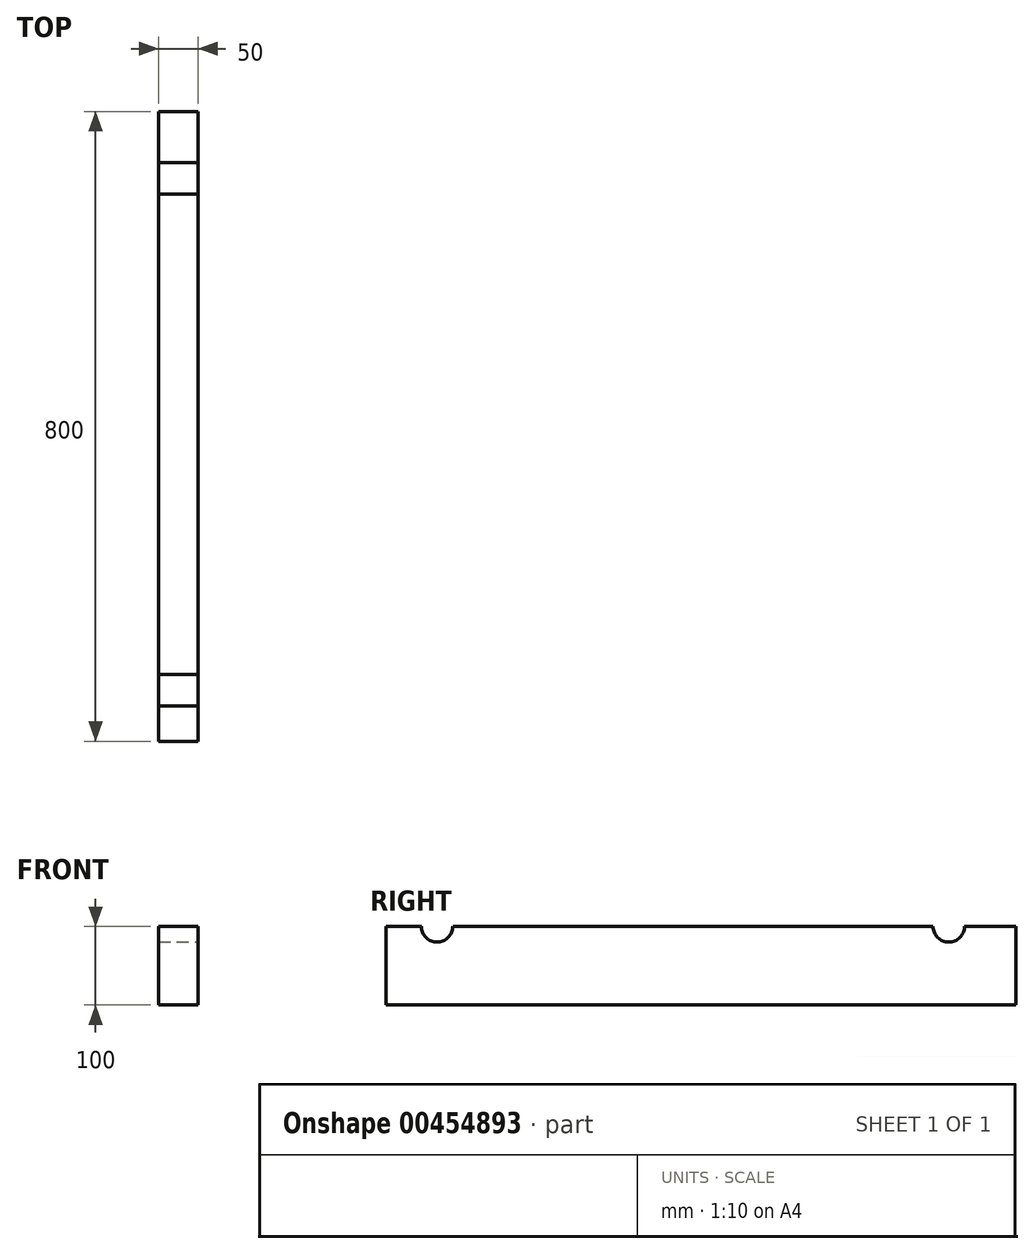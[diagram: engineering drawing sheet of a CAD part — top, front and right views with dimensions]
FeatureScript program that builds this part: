
annotation { "Feature Type Name" : "Feature", "Feature Type Description" : "" }
export const myFeature = defineFeature(function(context is Context, id is Id, definition is map)
    precondition{}
    {
        {
            var Q0;
            Q0=qCreatedBy(makeId("Front.planeOp"),FACE);
            var sketch = newSketch(context, id + "F0", { "sketchPlane" : qUnion([Q0])});
            skLineSegment(sketch, "E0.bottom", {"start": v(0, 0) * mm, "end": v(50, 0) * mm});
            skLineSegment(sketch, "E0.top", {"start": v(0, 100) * mm, "end": v(50, 100) * mm});
            skLineSegment(sketch, "E0.left", {"start": v(0, 0) * mm, "end": v(0, 100) * mm});
            skLineSegment(sketch, "E0.right", {"start": v(50, 0) * mm, "end": v(50, 100) * mm});
            skSolve(sketch);
        }
        {
            var Q0;
            Q0 = qSketchRegion(id + "F0", true);
            extrude(context, id + "F1", {"entities" : qUnion([Q0]), "depth" : 800 * mm});
        }
        {
            var Q0;
            Q0=makeQuery(id+"F1.opExtrude","SWEPT_FACE",FACE,{"disambiguationData":[OSD([sQuery(id+"F0.wireOp",EDGE,"E0.right")])]});
            var sketch = newSketch(context, id + "F2", { "sketchPlane" : qUnion([Q0])});
            skArc(sketch, "E1", {"start": v(-755, 100) * mm, "mid": v(-735, 80) * mm, "end": v(-715, 100) * mm});
            skArc(sketch, "E2", {"start": v(-105, 100) * mm, "mid": v(-85, 80) * mm, "end": v(-65, 100) * mm});
            skLineSegment(sketch, "E3", {"start": v(-755, 100) * mm, "end": v(-715, 100) * mm});
            skLineSegment(sketch, "E4", {"start": v(-105, 100) * mm, "end": v(-65, 100) * mm});
            skSolve(sketch);
        }
        {
            var Q0;
            Q0 = qSketchRegion(id + "F2", true);
            extrude(context, id + "F3", {"entities" : qUnion([Q0]), "operationType" : NewBodyOperationType.REMOVE, "endBound" : BoundingType.THROUGH_ALL, "oppositeDirection" : true, "depth" : 25 * mm});
        }
    });
